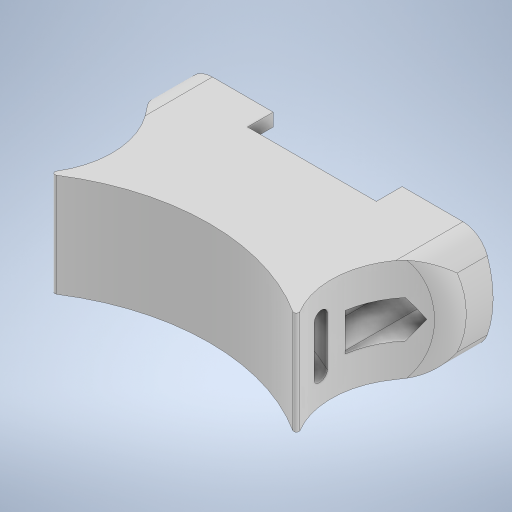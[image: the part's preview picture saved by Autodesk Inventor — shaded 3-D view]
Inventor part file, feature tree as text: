
AUTODESK INVENTOR PART (.ipt)
format: ipt  version: 2023 (Build 270158000, 158)  size: 454,144 bytes
history: native  units: mm
features: projected_geometry x9, extrude x8, sketch x8, fillet x3, other x2
ambient origin geometry x8: Origin, YZ Plane, XZ Plane, XY Plane, X Axis, Y Axis, Z Axis, Center Point
bodies: Body1 (feature_tree)
feature tree (30):
  other  "Těleso1"
  extrude  "Vysunutí1"  Depth=35.0mm
  extrude  "Vysunutí2"  Depth=20.0mm
  extrude  "Vysunutí3"  Depth=10.0mm TaperAngle=0.0deg
  extrude  "Vysunutí4"  Depth=15.0mm
  extrude  "Vysunutí5"  Depth=30.0mm
  other  "Rotace1"
  sketch  "Náčrt10"
  extrude  "Vysunutí9"  Depth=7.5mm TaperAngle=0.0deg
  extrude  "Vysunutí10"  Depth=5.0mm
  extrude  "Vysunutí11"  Depth=25.0mm
  fillet  "Zaoblení6"  [1 undecoded]
  fillet  "Zaoblení7"  Radius=20.0mm
  fillet  "Zaoblení9"  Radius=5.0mm
  sketch  "Náčrt1"
  sketch  "Náčrt2"
  projected_geometry  "Promítnutá smyčka1"
  sketch  "Náčrt3"
  projected_geometry  "Promítnutá smyčka2"
  sketch  "Náčrt4"
  projected_geometry  "Promítnutá smyčka3"
  projected_geometry  "Promítnutá smyčka4"
  sketch  "Náčrt6"
  projected_geometry  "Promítnutá smyčka8"
  sketch  "Náčrt7"
  projected_geometry  "Promítnutá smyčka11"
  projected_geometry  "Promítnutá smyčka12"
  sketch  "Náčrt11"
  projected_geometry  "Promítnutá smyčka13"
  projected_geometry  "Promítnutá smyčka14"
note: 1 required parameter value undecoded (feature->parameter linkage not recoverable at this tier; creation-order binding heuristic only, values carry confidence <= 0.55)
